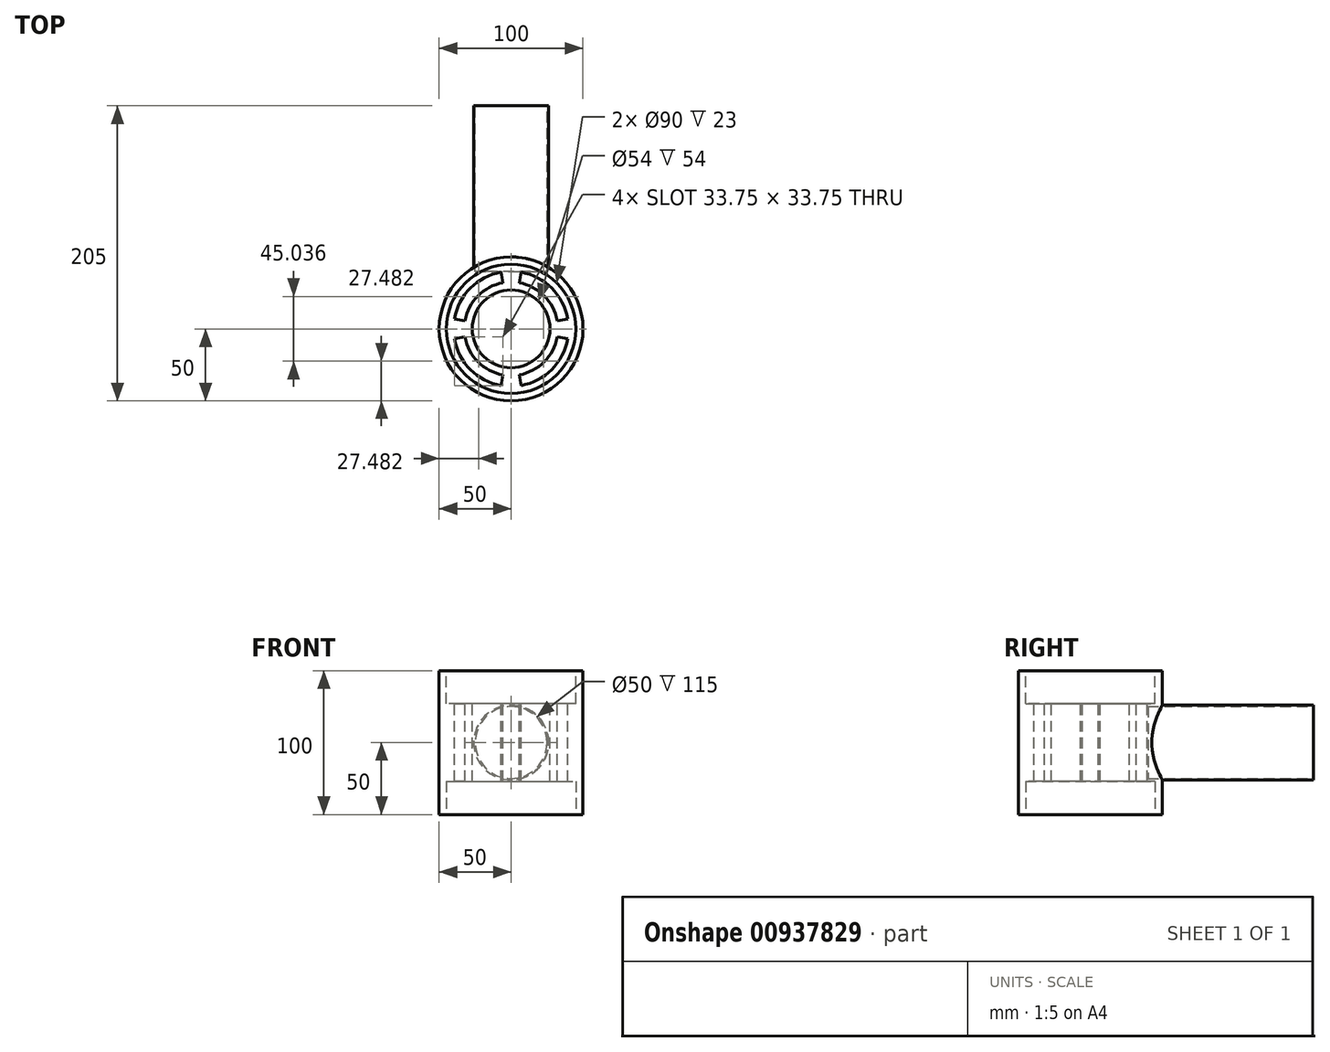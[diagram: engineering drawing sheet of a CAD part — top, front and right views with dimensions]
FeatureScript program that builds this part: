
annotation { "Feature Type Name" : "Feature", "Feature Type Description" : "" }
export const myFeature = defineFeature(function(context is Context, id is Id, definition is map)
    precondition{}
    {
        {
            var Q0;
            Q0=qCreatedBy(makeId("Front.planeOp"),FACE);
            var sketch = newSketch(context, id + "F0", { "sketchPlane" : qUnion([Q0])});
            skLineSegment(sketch, "E0", {"start": v(0, 0) * mm, "end": v(0, 0) * mm});
            skLineSegment(sketch, "E1.bottom", {"start": v(50, -50) * mm, "end": v(-50, -50) * mm});
            skLineSegment(sketch, "E1.top", {"start": v(50, 50) * mm, "end": v(-50, 50) * mm});
            skLineSegment(sketch, "E1.left", {"start": v(50, -50) * mm, "end": v(50, 50) * mm});
            skLineSegment(sketch, "E1.right", {"start": v(-50, -50) * mm, "end": v(-50, 50) * mm});
            skPoint(sketch, "E1.middle", {"position": v(0, 0) * mm});
            skSolve(sketch);
        }
        {
            var Q0;
            {var subQ1=sQuery(id+"F0.wireOp",EDGE,"E1.top");Q0=makeQuery(id+"F0.imprint","IMPRINT",FACE,{"disambiguationData":[TD([[makeQuery(id+"F0.imprint","IMPRINT",EDGE,{"derivedFrom":subQ1}),1.0]])]});}
            extrude(context, id + "F1", {"entities" : qUnion([Q0]), "depth" : 100 * mm, "offsetDistance" : 25 * mm, "symmetric" : true});
        }
        {
            var Q0;
            Q0=makeQuery(id+"F1.opExtrude","SWEPT_FACE",FACE,{"disambiguationData":[OSD([sQuery(id+"F0.wireOp",EDGE,"E1.top")])]});
            var sketch = newSketch(context, id + "F2", { "sketchPlane" : qUnion([Q0])});
            skCircle(sketch, "E2", {"center": v(0, 0) * mm, "radius": 27 * mm});
            skSolve(sketch);
        }
        {
            var Q0;
            Q0=qSketchRegion(id+"F2",true);
            extrude(context, id + "F3", {"entities" : qUnion([Q0]), "operationType" : NewBodyOperationType.REMOVE, "endBound" : BoundingType.THROUGH_ALL, "oppositeDirection" : true, "depth" : 50 * mm, "offsetDistance" : 25 * mm});
        }
        {
            var Q0;
            Q0=makeQuery(id+"F1.opExtrude","SWEPT_FACE",FACE,{"disambiguationData":[OSD([sQuery(id+"F0.wireOp",EDGE,"E1.top")])]});
            var sketch = newSketch(context, id + "F4", { "sketchPlane" : qUnion([Q0])});
            skCircle(sketch, "E3", {"center": v(0, 0) * mm, "radius": 45 * mm});
            skSolve(sketch);
        }
        {
            var Q0;
            Q0=qSketchRegion(id+"F4",true);
            extrude(context, id + "F5", {"entities" : qUnion([Q0]), "operationType" : NewBodyOperationType.REMOVE, "oppositeDirection" : true, "depth" : 23 * mm, "offsetDistance" : 25 * mm});
        }
        {
            var Q0;
            Q0=makeQuery(id+"F1.opExtrude","SWEPT_FACE",FACE,{"disambiguationData":[OSD([sQuery(id+"F0.wireOp",EDGE,"E1.bottom")])]});
            var sketch = newSketch(context, id + "F6", { "sketchPlane" : qUnion([Q0])});
            skCircle(sketch, "E4", {"center": v(0, 0) * mm, "radius": 45 * mm});
            skSolve(sketch);
        }
        {
            var Q0;
            Q0=makeQuery(id+"F6.imprint","IMPRINT",FACE,{"disambiguationData":[TD([[makeQuery(id+"F6.imprint","IMPRINT",EDGE,{"derivedFrom":sQuery(id+"F6.wireOp",EDGE,"E4")}),1.0]])]});
            var Q1;
            Q1=sQuery(id+"F6.wireOp",EDGE,"E4");
            extrude(context, id + "F7", {"entities" : qUnion([Q0]), "operationType" : NewBodyOperationType.REMOVE, "surfaceEntities" : qUnion([Q1]), "oppositeDirection" : true, "depth" : 23 * mm, "offsetDistance" : 25 * mm});
        }
        {
            var Q0;
            Q0=makeQuery(id+"F1.opExtrude","CAP_EDGE",EDGE,{"disambiguationData":[OSD([sQuery(id+"F0.wireOp",EDGE,"E1.left")])],"isStart":false});
            var Q1;
            Q1=makeQuery(id+"F1.opExtrude","CAP_EDGE",EDGE,{"disambiguationData":[OSD([sQuery(id+"F0.wireOp",EDGE,"E1.right")])],"isStart":false});
            fillet(context, id + "F8", {"entities" : qUnion([Q0, Q1]), "radius" : 50 * mm, "tangentPropagation" : true, "allowEdgeOverflow" : false});
        }
        {
            var Q0;
            Q0=makeQuery(id+"F1.opExtrude","CAP_FACE",FACE,{"disambiguationData":[OSD([sQuery(id+"F0.wireOp",EDGE,"E1.bottom"),sQuery(id+"F0.wireOp",EDGE,"E1.top"),sQuery(id+"F0.wireOp",EDGE,"E1.left"),sQuery(id+"F0.wireOp",EDGE,"E1.right")])],"isStart":true});
            var sketch = newSketch(context, id + "F9", { "sketchPlane" : qUnion([Q0])});
            skPoint(sketch, "E5", {"position": v(0, 0) * mm});
            skCircle(sketch, "E6", {"center": v(0, 0) * mm, "radius": 25 * mm});
            skSolve(sketch);
        }
        {
            var Q0;
            Q0=qSketchRegion(id+"F9",true);
            extrude(context, id + "F10", {"entities" : qUnion([Q0]), "operationType" : NewBodyOperationType.REMOVE, "oppositeDirection" : true, "depth" : 10 * mm, "offsetDistance" : 25 * mm});
        }
        {
            var Q0;
            Q0=makeQuery(id+"F1.opExtrude","CAP_FACE",FACE,{"disambiguationData":[OSD([sQuery(id+"F0.wireOp",EDGE,"E1.bottom"),sQuery(id+"F0.wireOp",EDGE,"E1.top"),sQuery(id+"F0.wireOp",EDGE,"E1.left"),sQuery(id+"F0.wireOp",EDGE,"E1.right")])],"isStart":true});
            var sketch = newSketch(context, id + "F11", { "sketchPlane" : qUnion([Q0])});
            skCircle(sketch, "E7", {"center": v(0, 0) * mm, "radius": 26 * mm});
            skSolve(sketch);
        }
        {
            var Q0;
            Q0=makeQuery(id+"F11.imprint","IMPRINT",FACE,{"disambiguationData":[TD([[makeQuery(id+"F11.imprint","IMPRINT",EDGE,{"derivedFrom":sQuery(id+"F11.wireOp",EDGE,"E7")}),1.0]])]});
            extrude(context, id + "F12", {"entities" : qUnion([Q0]), "operationType" : NewBodyOperationType.ADD, "depth" : 105 * mm, "offsetDistance" : 25 * mm});
        }
        {
            var Q0;
            Q0=makeQuery(id+"F1.opExtrude","CAP_EDGE",EDGE,{"disambiguationData":[OSD([sQuery(id+"F0.wireOp",EDGE,"E1.left")])],"isStart":true});
            var Q1;
            Q1=makeQuery(id+"F1.opExtrude","CAP_EDGE",EDGE,{"disambiguationData":[OSD([sQuery(id+"F0.wireOp",EDGE,"E1.right")])],"isStart":true});
            fillet(context, id + "F13", {"entities" : qUnion([Q0, Q1]), "radius" : 50 * mm, "tangentPropagation" : true, "allowEdgeOverflow" : false});
        }
        {
            var Q0;
            Q0=makeQuery(id+"F5.boolean.opBoolean","COPY",FACE,{"derivedFrom":makeQuery(id+"F5.opExtrude","CAP_FACE",FACE,{"disambiguationData":[OSD([sQuery(id+"F4.wireOp",EDGE,"E3")])],"isStart":false})});
            var sketch = newSketch(context, id + "F14", { "sketchPlane" : qUnion([Q0])});
            skCircle(sketch, "E8", {"center": v(0, 0) * mm, "radius": 32.5 * mm});
            skCircle(sketch, "E9", {"center": v(0, 0) * mm, "radius": 40 * mm});
            skLineSegment(sketch, "E10", {"start": v(-39.4, -6.95) * mm, "end": v(0, 0) * mm});
            skLineSegment(sketch, "E11", {"start": v(-6.95, 39.4) * mm, "end": v(0, 0) * mm});
            skLineSegment(sketch, "E12", {"start": v(6.95, 39.4) * mm, "end": v(0, 0) * mm});
            skLineSegment(sketch, "E13", {"start": v(6.95, -39.4) * mm, "end": v(0, 0) * mm});
            skLineSegment(sketch, "E14", {"start": v(-39.4, 6.95) * mm, "end": v(0, 0) * mm});
            skLineSegment(sketch, "E15", {"start": v(-6.95, -39.4) * mm, "end": v(0, 0) * mm});
            skLineSegment(sketch, "E16", {"start": v(39.4, 6.95) * mm, "end": v(0, 0) * mm});
            skLineSegment(sketch, "E17", {"start": v(39.4, -6.95) * mm, "end": v(0, 0) * mm});
            skSolve(sketch);
        }
        {
            var Q0;
            {var subQ0=sQuery(id+"F14.wireOp",EDGE,"E11");var subQ1=sQuery(id+"F14.wireOp",EDGE,"E8");var subQ2=makeQuery(id+"F14.imprint","INTERSECT",VERTEX,{"derivedFrom":[subQ1,subQ0]});Q0=makeQuery(id+"F14.imprint","IMPRINT",FACE,{"disambiguationData":[TD([[makeQuery(id+"F14.imprint","IMPRINT",EDGE,{"disambiguationData":[TD([[subQ2,-1.0]])],"derivedFrom":subQ1}),-1.0]])]});}
            var Q1;
            {var subQ0=sQuery(id+"F14.wireOp",EDGE,"E12");var subQ1=sQuery(id+"F14.wireOp",EDGE,"E8");var subQ2=makeQuery(id+"F14.imprint","INTERSECT",VERTEX,{"derivedFrom":[subQ1,subQ0]});Q1=makeQuery(id+"F14.imprint","IMPRINT",FACE,{"disambiguationData":[TD([[makeQuery(id+"F14.imprint","IMPRINT",EDGE,{"disambiguationData":[TD([[subQ2,1.0]])],"derivedFrom":subQ1}),-1.0]])]});}
            var Q2;
            {var subQ0=sQuery(id+"F14.wireOp",EDGE,"E13");var subQ1=sQuery(id+"F14.wireOp",EDGE,"E8");var subQ2=makeQuery(id+"F14.imprint","INTERSECT",VERTEX,{"derivedFrom":[subQ1,subQ0]});Q2=makeQuery(id+"F14.imprint","IMPRINT",FACE,{"disambiguationData":[TD([[makeQuery(id+"F14.imprint","IMPRINT",EDGE,{"disambiguationData":[TD([[subQ2,-1.0]])],"derivedFrom":subQ1}),-1.0]])]});}
            var Q3;
            {var subQ0=sQuery(id+"F14.wireOp",EDGE,"E10");var subQ1=sQuery(id+"F14.wireOp",EDGE,"E8");var subQ2=makeQuery(id+"F14.imprint","INTERSECT",VERTEX,{"derivedFrom":[subQ1,subQ0]});Q3=makeQuery(id+"F14.imprint","IMPRINT",FACE,{"disambiguationData":[TD([[makeQuery(id+"F14.imprint","IMPRINT",EDGE,{"disambiguationData":[TD([[subQ2,-1.0]])],"derivedFrom":subQ1}),-1.0]])]});}
            extrude(context, id + "F15", {"entities" : qUnion([Q0, Q1, Q2, Q3]), "operationType" : NewBodyOperationType.REMOVE, "endBound" : BoundingType.THROUGH_ALL, "oppositeDirection" : true, "depth" : 25 * mm, "offsetDistance" : 25 * mm});
        }
    });
